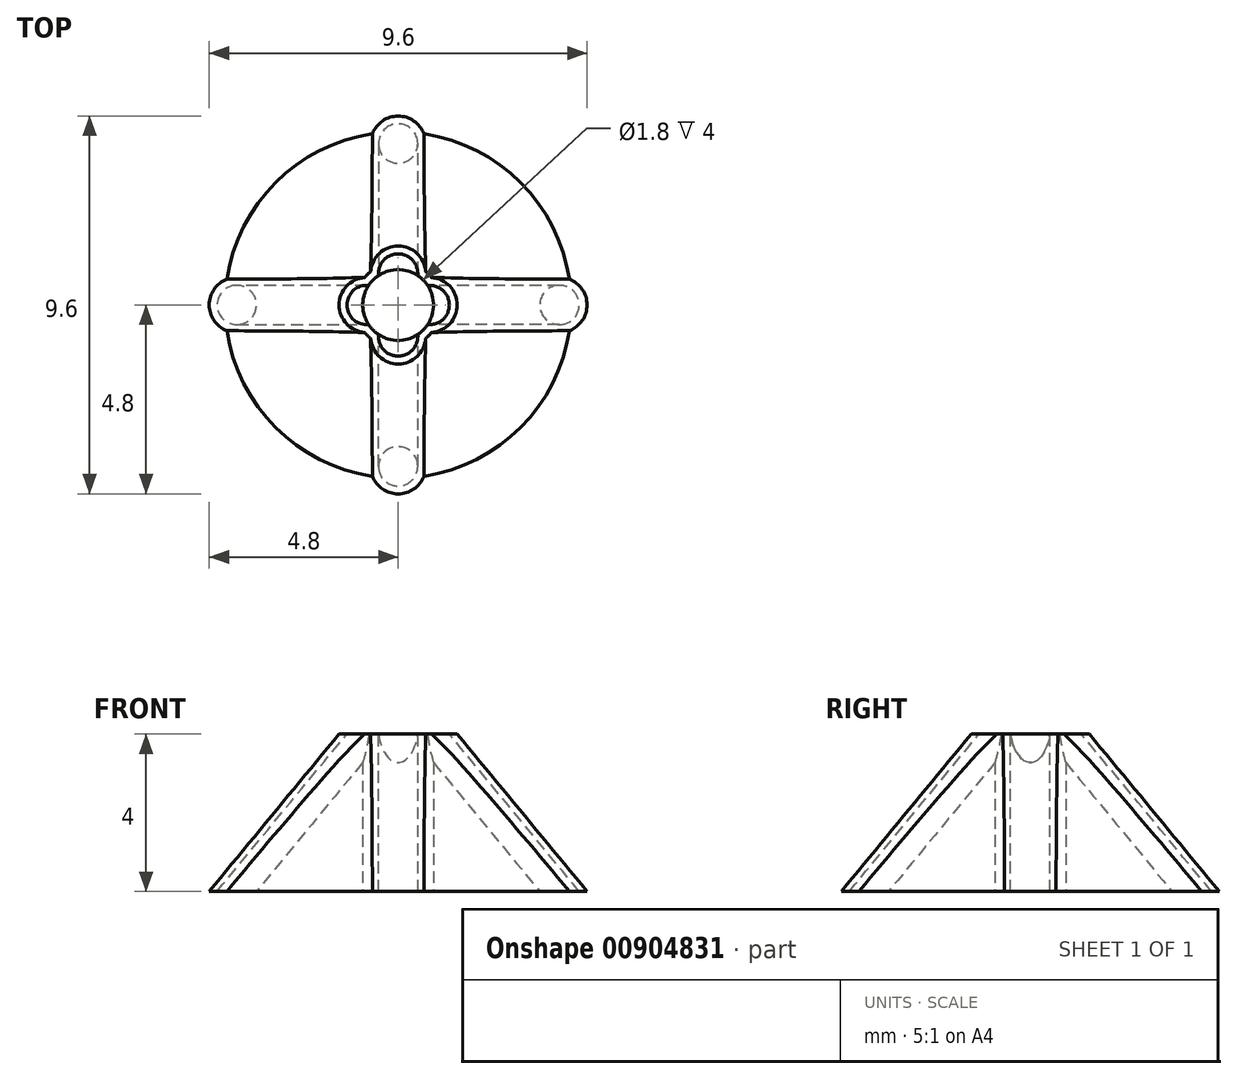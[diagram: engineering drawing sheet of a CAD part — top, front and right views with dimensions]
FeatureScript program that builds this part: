
annotation { "Feature Type Name" : "Feature", "Feature Type Description" : "" }
export const myFeature = defineFeature(function(context is Context, id is Id, definition is map)
    precondition{}
    {
        {
            var Q0;
            Q0=qCreatedBy(makeId("Front.planeOp"),FACE);
            var sketch = newSketch(context, id + "F0", { "sketchPlane" : qUnion([Q0])});
            skLineSegment(sketch, "E0", {"start": v(-0.8, 4) * mm, "end": v(-0.8, 0) * mm});
            skLineSegment(sketch, "E1", {"start": v(-0.8, 0) * mm, "end": v(-4.4, 0) * mm});
            skLineSegment(sketch, "E2", {"start": v(-0.8, 0) * mm, "end": v(0, 0) * mm, "construction": true});
            skLineSegment(sketch, "E3", {"start": v(0, 0) * mm, "end": v(0, 4) * mm, "construction": true});
            skLineSegment(sketch, "E4", {"start": v(0, 4) * mm, "end": v(-0.8, 4) * mm, "construction": true});
            skLineSegment(sketch, "E5", {"start": v(-0.8, 4) * mm, "end": v(-1.1, 4) * mm});
            skLineSegment(sketch, "E6", {"start": v(-1.1, 4) * mm, "end": v(-4.4, 0) * mm});
            skSolve(sketch);
        }
        {
            var Q0;
            Q0=makeQuery(id+"F0.imprint","IMPRINT",FACE,{"disambiguationData":[TD([[makeQuery(id+"F0.imprint","IMPRINT",EDGE,{"derivedFrom":sQuery(id+"F0.wireOp",EDGE,"E0")}),-1.0]])]});
            var Q1;
            Q1=sQuery(id+"F0.wireOp",EDGE,"E3");
            revolve(context, id + "F1", {"surfaceOperationType" : NewSurfaceOperationType.NEW, "entities" : qUnion([Q0]), "axis" : qUnion([Q1]), "revolveType" : RevolveType.FULL});
        }
        {
            var Q0;
            Q0=makeQuery(id+"F1.opRevolve","SWEPT_FACE",FACE,{"disambiguationData":[OSD([sQuery(id+"F0.wireOp",EDGE,"E5")])]});
            var sketch = newSketch(context, id + "F2", { "sketchPlane" : qUnion([Q0])});
            skCircle(sketch, "E7", {"center": v(0, 0.8) * mm, "radius": 0.7 * mm});
            skCircle(sketch, "E8", {"center": v(0, 0.8) * mm, "radius": 0.5 * mm});
            skSolve(sketch);
        }
        {
            var Q0;
            Q0=makeQuery(id+"F1.opRevolve","SWEPT_FACE",FACE,{"disambiguationData":[OSD([sQuery(id+"F0.wireOp",EDGE,"E6")])]});
            cPlane(context, id + "F3", {"entities" : qUnion([Q0]), "cplaneType" : CPlaneType.LINE_ANGLE, "offset" : 25 * mm, "angle" : 0 * degree, "width" : 150 * mm, "height" : 150 * mm});
        }
        {
            var Q0;
            Q0=qCreatedBy(id+"F3.planeOp",FACE);
            var sketch = newSketch(context, id + "F4", { "sketchPlane" : qUnion([Q0])});
            skLineSegment(sketch, "E9", {"start": v(1.1, 4) * mm, "end": v(4.4, 0) * mm});
            skLineSegment(sketch, "E10", {"start": v(-4.4, 0) * mm, "end": v(-1.1, 4) * mm});
            skLineSegment(sketch, "E11", {"start": v(-0.9, 5) * mm, "end": v(-4.4, 0) * mm});
            skLineSegment(sketch, "E12", {"start": v(0, 0) * mm, "end": v(0, 5) * mm, "construction": true});
            skLineSegment(sketch, "E13", {"start": v(0, 5) * mm, "end": v(-0.9, 5) * mm, "construction": true});
            skSolve(sketch);
        }
        {
            var Q0;
            {var subQ0=sQuery(id+"F2.wireOp",EDGE,"E7");var subQ1=makeQuery(id+"F1.opRevolve","SWEPT_EDGE",EDGE,{"disambiguationData":[OSD([sQuery(id+"F0.wireOp",EDGE,"E5"),sQuery(id+"F0.wireOp",EDGE,"E6")])]});var subQ2=makeQuery(id+"F2.imprint","INTERSECT",VERTEX,{"disambiguationData":[OD(0.0)],"derivedFrom":[subQ1,subQ0]});Q0=makeQuery(id+"F2.imprint","IMPRINT",FACE,{"disambiguationData":[TD([[makeQuery(id+"F2.imprint","IMPRINT",EDGE,{"disambiguationData":[TD([[subQ2,1.0]])],"derivedFrom":subQ0}),1.0]])]});}
            var Q1;
            {var subQ0=sQuery(id+"F2.wireOp",EDGE,"E7");var subQ1=sQuery(id+"F0.wireOp",EDGE,"E5");var subQ2=makeQuery(id+"F1.opRevolve","SWEPT_EDGE",EDGE,{"disambiguationData":[OSD([subQ1,sQuery(id+"F0.wireOp",EDGE,"E6")])]});var subQ3=makeQuery(id+"F2.imprint","INTERSECT",VERTEX,{"disambiguationData":[OD(0.0)],"derivedFrom":[subQ2,subQ0]});Q1=makeQuery(id+"F2.imprint","IMPRINT",FACE,{"disambiguationData":[TD([[makeQuery(id+"F2.imprint","IMPRINT",EDGE,{"disambiguationData":[TD([[subQ3,-1.0]])],"derivedFrom":subQ0}),1.0]])]});}
            var Q2;
            {var subQ0=sQuery(id+"F2.wireOp",EDGE,"E7");var subQ1=makeQuery(id+"F1.opRevolve","SWEPT_EDGE",EDGE,{"disambiguationData":[OSD([sQuery(id+"F0.wireOp",EDGE,"E0"),sQuery(id+"F0.wireOp",EDGE,"E5")])]});var subQ2=makeQuery(id+"F2.imprint","INTERSECT",VERTEX,{"disambiguationData":[OD(0.0)],"derivedFrom":[subQ1,subQ0]});Q2=makeQuery(id+"F2.imprint","IMPRINT",FACE,{"disambiguationData":[TD([[makeQuery(id+"F2.imprint","IMPRINT",EDGE,{"disambiguationData":[TD([[subQ2,-1.0]])],"derivedFrom":subQ0}),1.0]])]});}
            var Q3;
            {var subQ0=sQuery(id+"F2.wireOp",EDGE,"E7");var subQ1=sQuery(id+"F0.wireOp",EDGE,"E5");var subQ2=makeQuery(id+"F1.opRevolve","SWEPT_EDGE",EDGE,{"disambiguationData":[OSD([subQ1,sQuery(id+"F0.wireOp",EDGE,"E6")])]});var subQ3=makeQuery(id+"F2.imprint","INTERSECT",VERTEX,{"disambiguationData":[OD(1.0)],"derivedFrom":[subQ2,subQ0]});Q3=makeQuery(id+"F2.imprint","IMPRINT",FACE,{"disambiguationData":[TD([[makeQuery(id+"F2.imprint","IMPRINT",EDGE,{"disambiguationData":[TD([[subQ3,1.0]])],"derivedFrom":subQ0}),1.0]])]});}
            var Q4;
            Q4=sQuery(id+"F4.wireOp",EDGE,"E10");
            sweep(context, id + "F5", {"profiles" : qUnion([Q0, Q1, Q2, Q3]), "path" : qUnion([Q4])});
        }
        {
            var Q0;
            {var subQ0=sQuery(id+"F2.wireOp",EDGE,"E8");var subQ1=makeQuery(id+"F1.opRevolve","SWEPT_EDGE",EDGE,{"disambiguationData":[OSD([sQuery(id+"F0.wireOp",EDGE,"E5"),sQuery(id+"F0.wireOp",EDGE,"E6")])]});var subQ2=makeQuery(id+"F2.imprint","INTERSECT",VERTEX,{"disambiguationData":[OD(0.0)],"derivedFrom":[subQ1,subQ0]});Q0=makeQuery(id+"F2.imprint","IMPRINT",FACE,{"disambiguationData":[TD([[makeQuery(id+"F2.imprint","IMPRINT",EDGE,{"disambiguationData":[TD([[subQ2,1.0]])],"derivedFrom":subQ0}),1.0]])]});}
            var Q1;
            {var subQ0=sQuery(id+"F2.wireOp",EDGE,"E8");var subQ1=makeQuery(id+"F1.opRevolve","SWEPT_EDGE",EDGE,{"disambiguationData":[OSD([sQuery(id+"F0.wireOp",EDGE,"E0"),sQuery(id+"F0.wireOp",EDGE,"E5")])]});var subQ2=makeQuery(id+"F2.imprint","INTERSECT",VERTEX,{"disambiguationData":[OD(0.0)],"derivedFrom":[subQ1,subQ0]});Q1=makeQuery(id+"F2.imprint","IMPRINT",FACE,{"disambiguationData":[TD([[makeQuery(id+"F2.imprint","IMPRINT",EDGE,{"disambiguationData":[TD([[subQ2,-1.0]])],"derivedFrom":subQ0}),1.0]])]});}
            var Q2;
            {var subQ0=sQuery(id+"F2.wireOp",EDGE,"E8");var subQ1=sQuery(id+"F0.wireOp",EDGE,"E5");var subQ2=makeQuery(id+"F1.opRevolve","SWEPT_EDGE",EDGE,{"disambiguationData":[OSD([subQ1,sQuery(id+"F0.wireOp",EDGE,"E6")])]});var subQ3=makeQuery(id+"F2.imprint","INTERSECT",VERTEX,{"disambiguationData":[OD(0.0)],"derivedFrom":[subQ2,subQ0]});Q2=makeQuery(id+"F2.imprint","IMPRINT",FACE,{"disambiguationData":[TD([[makeQuery(id+"F2.imprint","IMPRINT",EDGE,{"disambiguationData":[TD([[subQ3,-1.0]])],"derivedFrom":subQ0}),1.0]])]});}
            var Q3;
            Q3=sQuery(id+"F4.wireOp",EDGE,"E10");
            sweep(context, id + "F6", {"operationType" : NewBodyOperationType.REMOVE, "profiles" : qUnion([Q0, Q1, Q2]), "path" : qUnion([Q3])});
        }
        {
            var Q0;
            Q0=makeQuery(id+"F5.opSweep","SWEPT_BODY",BODY,{"disambiguationData":[OSD([sQuery(id+"F2.wireOp",EDGE,"E7"),sQuery(id+"F2.wireOp",EDGE,"E8"),sQuery(id+"F4.wireOp",EDGE,"E10")])]});
            var Q1;
            Q1=makeQuery(id+"F6.boolean.opBoolean","COPY",FACE,{"derivedFrom":makeQuery(id+"F6.opSweep","SWEPT_FACE",FACE,{"disambiguationData":[OSD([sQuery(id+"F2.wireOp",EDGE,"E8"),sQuery(id+"F4.wireOp",EDGE,"E10")])]})});
            var Q2;
            Q2=makeQuery(id+"F1.opRevolve","SWEPT_FACE",FACE,{"disambiguationData":[OSD([sQuery(id+"F0.wireOp",EDGE,"E6")])]});
            circularPattern(context, id + "F7", {"patternType" : PatternType.FACE, "faces" : qUnion([Q1]), "axis" : qUnion([Q2]), "angle" : 360 * degree, "instanceCount" : 4, "equalSpace" : true});
        }
        {
            var Q0;
            Q0=makeQuery(id+"F5.opSweep","SWEPT_BODY",BODY,{"disambiguationData":[OSD([sQuery(id+"F2.wireOp",EDGE,"E7"),sQuery(id+"F2.wireOp",EDGE,"E8"),sQuery(id+"F4.wireOp",EDGE,"E10")])]});
            var Q1;
            Q1=makeQuery(id+"F1.opRevolve","SWEPT_FACE",FACE,{"disambiguationData":[OSD([sQuery(id+"F0.wireOp",EDGE,"E0")])]});
            circularPattern(context, id + "F8", {"entities" : qUnion([Q0]), "axis" : qUnion([Q1]), "angle" : 360 * degree, "instanceCount" : 4, "equalSpace" : true});
        }
        {
            var Q0;
            Q0=makeQuery(id+"F8.opPattern","COPY",BODY,{"derivedFrom":makeQuery(id+"F5.opSweep","SWEPT_BODY",BODY,{"disambiguationData":[OSD([sQuery(id+"F2.wireOp",EDGE,"E7"),sQuery(id+"F2.wireOp",EDGE,"E8"),sQuery(id+"F4.wireOp",EDGE,"E10")])]}),"instanceName":"2"});
            var Q1;
            Q1=makeQuery(id+"F8.opPattern","COPY",BODY,{"derivedFrom":makeQuery(id+"F5.opSweep","SWEPT_BODY",BODY,{"disambiguationData":[OSD([sQuery(id+"F2.wireOp",EDGE,"E7"),sQuery(id+"F2.wireOp",EDGE,"E8"),sQuery(id+"F4.wireOp",EDGE,"E10")])]}),"instanceName":"3"});
            var Q2;
            Q2=makeQuery(id+"F5.opSweep","SWEPT_BODY",BODY,{"disambiguationData":[OSD([sQuery(id+"F2.wireOp",EDGE,"E7"),sQuery(id+"F2.wireOp",EDGE,"E8"),sQuery(id+"F4.wireOp",EDGE,"E10")])]});
            var Q3;
            Q3=makeQuery(id+"F8.opPattern","COPY",BODY,{"derivedFrom":makeQuery(id+"F5.opSweep","SWEPT_BODY",BODY,{"disambiguationData":[OSD([sQuery(id+"F2.wireOp",EDGE,"E7"),sQuery(id+"F2.wireOp",EDGE,"E8"),sQuery(id+"F4.wireOp",EDGE,"E10")])]}),"instanceName":"1"});
            var Q4;
            Q4=makeQuery(id+"F1.opRevolve","SWEPT_BODY",BODY,{"disambiguationData":[OSD([sQuery(id+"F0.wireOp",EDGE,"E0"),sQuery(id+"F0.wireOp",EDGE,"E1"),sQuery(id+"F0.wireOp",EDGE,"E5"),sQuery(id+"F0.wireOp",EDGE,"E6")])]});
            booleanBodies(context, id + "F9", {"operationType" : BooleanOperationType.UNION, "tools" : qUnion([Q0, Q1, Q2, Q3, Q4])});
        }
        {
            var Q0;
            {var subQ0=makeQuery(id+"F5.opSweep","CAP_FACE",FACE,{"disambiguationData":[OSD([sQuery(id+"F2.wireOp",EDGE,"E7"),sQuery(id+"F2.wireOp",EDGE,"E8"),sQuery(id+"F4.wireOp",VERTEX,"E10.start")])],"isStart":false});Q0=makeQuery(id+"F9.opBoolean","MERGE",FACE,{"derivedFrom":[subQ0,makeQuery(id+"F1.opRevolve","SWEPT_FACE",FACE,{"disambiguationData":[OSD([sQuery(id+"F0.wireOp",EDGE,"E1")])]}),makeQuery(id+"F8.opPattern","COPY",FACE,{"derivedFrom":subQ0,"instanceName":"1"}),makeQuery(id+"F8.opPattern","COPY",FACE,{"derivedFrom":subQ0,"instanceName":"2"}),makeQuery(id+"F8.opPattern","COPY",FACE,{"derivedFrom":subQ0,"instanceName":"3"})]});}
            var sketch = newSketch(context, id + "F10", { "sketchPlane" : qUnion([Q0])});
            skCircle(sketch, "E14", {"center": v(0, 0) * mm, "radius": 0.9 * mm});
            skSolve(sketch);
        }
        {
            var Q0;
            Q0 = qSketchRegion(id + "F10", true);
            extrude(context, id + "F11", {"entities" : qUnion([Q0]), "operationType" : NewBodyOperationType.REMOVE, "oppositeDirection" : true, "depth" : 4 * mm, "offsetDistance" : 25 * mm});
        }
    });
